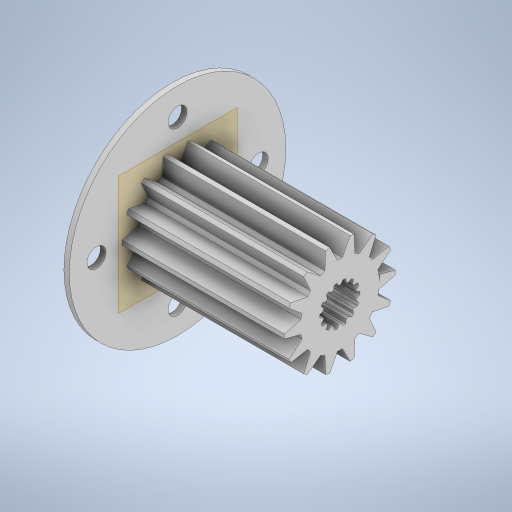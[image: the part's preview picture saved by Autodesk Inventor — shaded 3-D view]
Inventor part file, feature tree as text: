
AUTODESK INVENTOR PART (.ipt)
format: ipt  version: 2023 (Build 270158000, 158)  size: 470,016 bytes
history: native  units: mm
features: sketch x3, extrude x3, plane x2
ambient origin geometry x8: Origin, YZ Plane, XZ Plane, XY Plane, X Axis, Y Axis, Z Axis, Center Point
bodies: Solid1 (feature_tree)
feature tree (8):
  sketch  "Sketch1"  dims[d0=30.0mm d1=3.5mm]
  plane  "Work Plane1"
  plane  "Work Plane2"
  extrude  "Extrusion2"  Depth=30.0mm
  extrude  "Extrusion3"  Depth=40.0mm
  extrude  "Extrusion4"  TaperAngle=360.0deg  [1 undecoded]
  sketch  "Sketch3"  dims[d10=140.0mm d11=360.0deg d12=14.6304mm d14=1.168mm d15=3.0226mm d16=2.584833mm d17=140.0mm d19=360.0deg d21=30.0mm d22=0.0mm d23=30.0mm d24=0.0mm d25=3.5mm d26=1.0mm d27=0.0mm]
  sketch  "Sketch2"  dims[d2=40.0mm d4=360.0deg d6=40.0mm]
note: 1 required parameter value undecoded (feature->parameter linkage not recoverable at this tier; creation-order binding heuristic only, values carry confidence <= 0.55)
